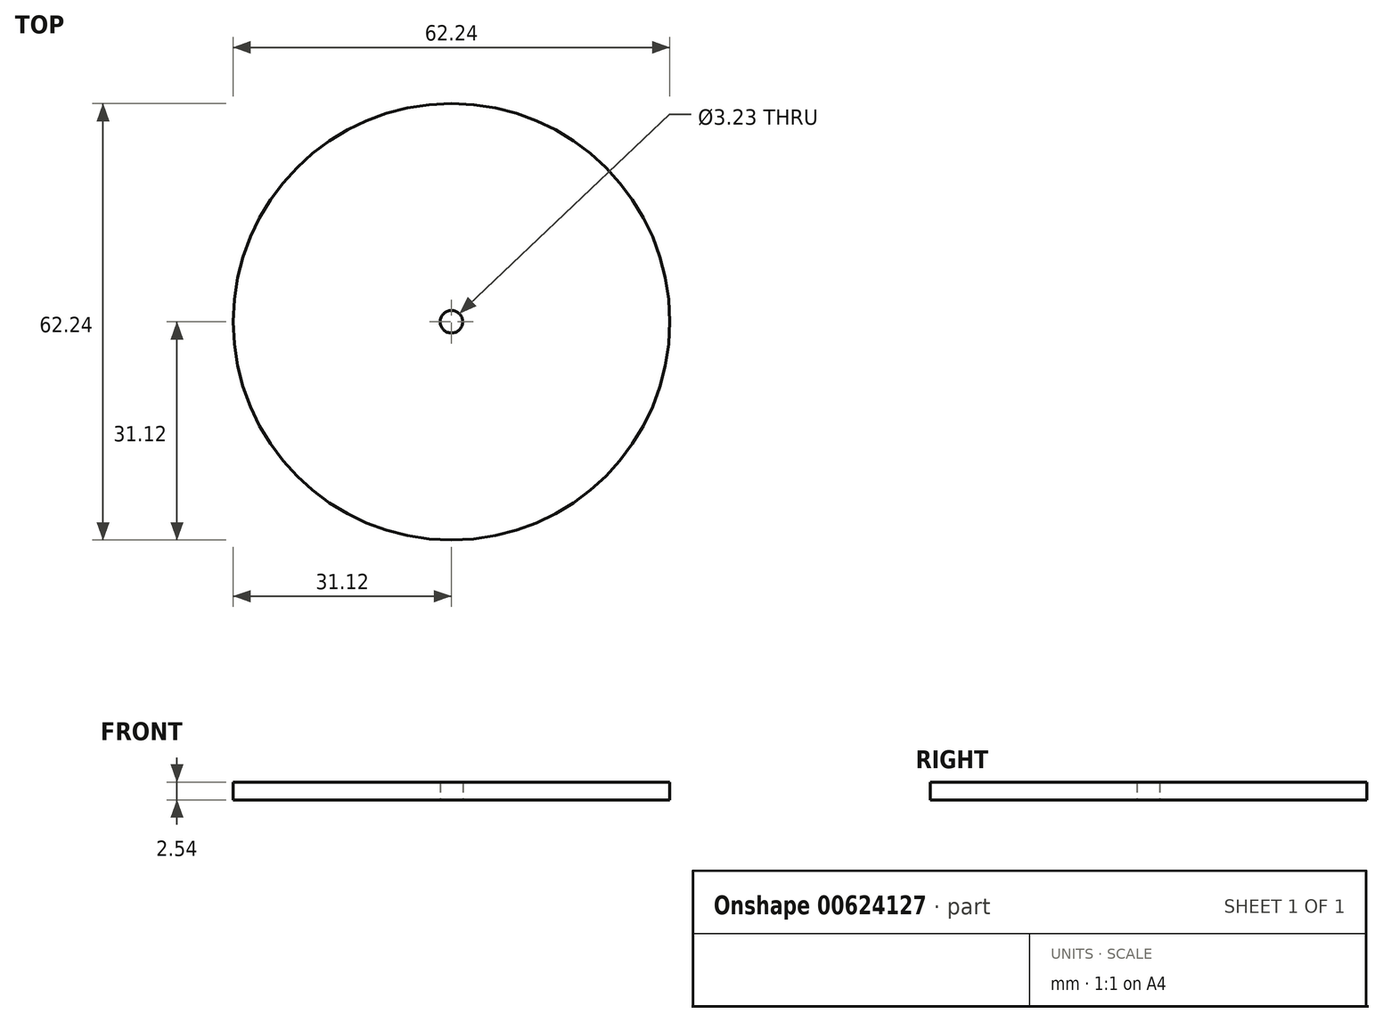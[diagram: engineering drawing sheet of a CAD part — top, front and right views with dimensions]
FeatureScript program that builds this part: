
annotation { "Feature Type Name" : "Feature", "Feature Type Description" : "" }
export const myFeature = defineFeature(function(context is Context, id is Id, definition is map)
    precondition{}
    {
        {
            var Q0;
            Q0=qCreatedBy(makeId("Top.planeOp"),FACE);
            var sketch = newSketch(context, id + "F0", { "sketchPlane" : qUnion([Q0])});
            skCircle(sketch, "E0", {"center": v(0, 0) * mm, "radius": 31.12 * mm});
            skCircle(sketch, "E1", {"center": v(0, 0) * mm, "radius": 1.61 * mm});
            skSolve(sketch);
        }
        {
            var Q0;
            Q0 = qSketchRegion(id + "F0", true);
            extrude(context, id + "F1", {"entities" : qUnion([Q0]), "depth" : 2.54 * mm, "offsetDistance" : 25.4 * mm});
        }
    });
